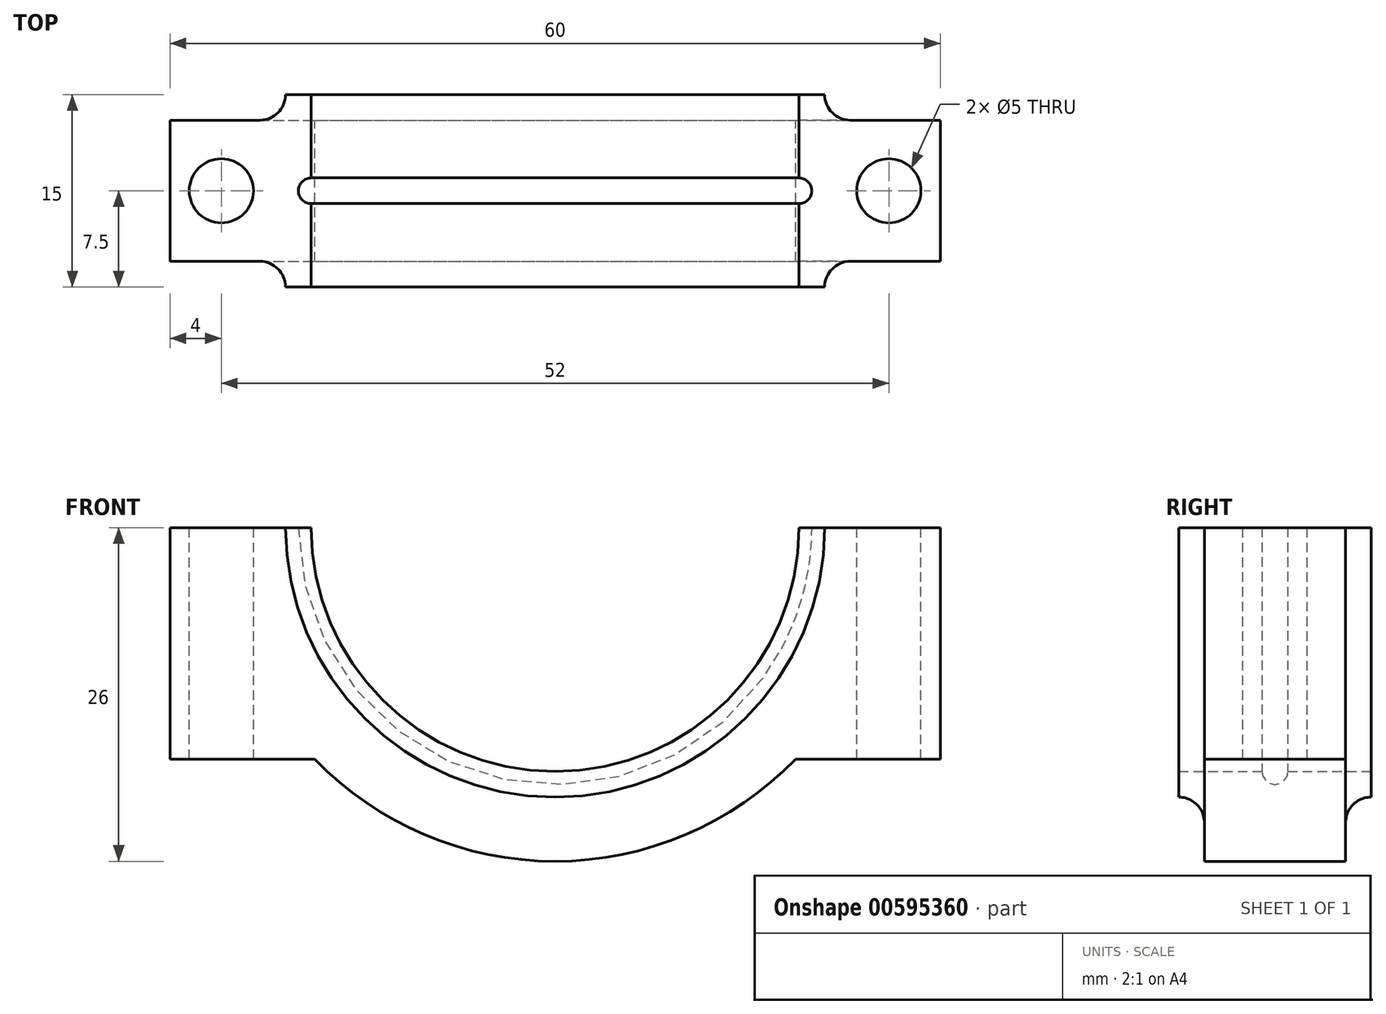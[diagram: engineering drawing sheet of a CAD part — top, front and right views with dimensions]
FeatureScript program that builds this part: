
annotation { "Feature Type Name" : "Feature", "Feature Type Description" : "" }
export const myFeature = defineFeature(function(context is Context, id is Id, definition is map)
    precondition{}
    {
        {
            var Q0;
            Q0=qCreatedBy(makeId("Front.planeOp"),FACE);
            var sketch = newSketch(context, id + "F0", { "sketchPlane" : qUnion([Q0])});
            skArc(sketch, "E0", {"start": v(-19, 0) * mm, "mid": v(0, -19) * mm, "end": v(19, 0) * mm});
            skLineSegment(sketch, "E1", {"start": v(-67.76, 0) * mm, "end": v(69.48, 0) * mm, "construction": true});
            skLineSegment(sketch, "E2", {"start": v(-30, 0) * mm, "end": v(-30, -18.03) * mm});
            skLineSegment(sketch, "E3.MirrorCS", {"start": v(30, 0) * mm, "end": v(30, -18.03) * mm});
            skLineSegment(sketch, "E4", {"start": v(-30, 0) * mm, "end": v(-19, 0) * mm});
            skLineSegment(sketch, "E5", {"start": v(19, 0) * mm, "end": v(30, 0) * mm});
            skArc(sketch, "E6", {"start": v(-18.73, -18.03) * mm, "mid": v(0, -26) * mm, "end": v(18.73, -18.03) * mm});
            skLineSegment(sketch, "E7", {"start": v(-30, -18.03) * mm, "end": v(-18.73, -18.03) * mm});
            skLineSegment(sketch, "E8", {"start": v(30, -18.03) * mm, "end": v(18.73, -18.03) * mm});
            skSolve(sketch);
        }
        {
            var Q0;
            Q0 = qSketchRegion(id + "F0", true);
            extrude(context, id + "F1", {"entities" : qUnion([Q0]), "endBound" : BoundingType.SYMMETRIC, "depth" : 11 * mm, "offsetDistance" : 25 * mm});
        }
        {
            var Q0;
            Q0=makeQuery(id+"F1.opExtrude","CAP_FACE",FACE,{"disambiguationData":[OSD([sQuery(id+"F0.wireOp",EDGE,"E0"),sQuery(id+"F0.wireOp",EDGE,"E2"),sQuery(id+"F0.wireOp",EDGE,"E3.MirrorCS"),sQuery(id+"F0.wireOp",EDGE,"E4"),sQuery(id+"F0.wireOp",EDGE,"E5"),sQuery(id+"F0.wireOp",EDGE,"E6"),sQuery(id+"F0.wireOp",EDGE,"E7"),sQuery(id+"F0.wireOp",EDGE,"E8")])],"isStart":false});
            var sketch = newSketch(context, id + "F2", { "sketchPlane" : qUnion([Q0])});
            skArc(sketch, "E9", {"start": v(-19, 0) * mm, "mid": v(0, -19) * mm, "end": v(19, 0) * mm});
            skArc(sketch, "E10", {"start": v(-21, 0) * mm, "mid": v(0, -21) * mm, "end": v(21, 0) * mm});
            skLineSegment(sketch, "E11", {"start": v(-26.55, 0) * mm, "end": v(28.6, 0) * mm, "construction": true});
            skLineSegment(sketch, "E12", {"start": v(-21, 0) * mm, "end": v(-19, 0) * mm});
            skLineSegment(sketch, "E13", {"start": v(19, 0) * mm, "end": v(21, 0) * mm});
            skSolve(sketch);
        }
        {
            var Q0;
            Q0 = qSketchRegion(id + "F2", true);
            extrude(context, id + "F3", {"entities" : qUnion([Q0]), "operationType" : NewBodyOperationType.ADD, "depth" : 2 * mm, "offsetDistance" : 25 * mm, "hasSecondDirection" : true, "secondDirectionOppositeDirection" : true, "secondDirectionDepth" : 13 * mm});
        }
        {
            var Q0;
            Q0=makeQuery(id+"F1.opExtrude","SWEPT_FACE",FACE,{"disambiguationData":[OSD([sQuery(id+"F0.wireOp",EDGE,"E4")])]});
            var sketch = newSketch(context, id + "F4", { "sketchPlane" : qUnion([Q0])});
            skCircle(sketch, "E14", {"center": v(-26, 0) * mm, "radius": 2.5 * mm});
            skCircle(sketch, "E15.MirrorC", {"center": v(26, 0) * mm, "radius": 2.5 * mm});
            skSolve(sketch);
        }
        {
            var Q0;
            Q0 = qSketchRegion(id + "F4", true);
            extrude(context, id + "F5", {"entities" : qUnion([Q0]), "operationType" : NewBodyOperationType.REMOVE, "endBound" : BoundingType.THROUGH_ALL, "oppositeDirection" : true, "depth" : 25 * mm, "offsetDistance" : 25 * mm});
        }
        {
            var Q0;
            Q0=makeQuery(id+"F3.boolean.opBoolean","INTERSECT",EDGE,{"derivedFrom":[makeQuery(id+"F1.opExtrude","CAP_FACE",FACE,{"disambiguationData":[OSD([sQuery(id+"F0.wireOp",EDGE,"E0"),sQuery(id+"F0.wireOp",EDGE,"E2"),sQuery(id+"F0.wireOp",EDGE,"E3.MirrorCS"),sQuery(id+"F0.wireOp",EDGE,"E4"),sQuery(id+"F0.wireOp",EDGE,"E5"),sQuery(id+"F0.wireOp",EDGE,"E6"),sQuery(id+"F0.wireOp",EDGE,"E7"),sQuery(id+"F0.wireOp",EDGE,"E8")])],"isStart":true}),makeQuery(id+"F3.opExtrude","SWEPT_FACE",FACE,{"disambiguationData":[OSD([sQuery(id+"F2.wireOp",EDGE,"E10")])]})]});
            fillet(context, id + "F6", {"entities" : qUnion([Q0]), "radius" : 2 * mm, "tangentPropagation" : true, "allowEdgeOverflow" : false});
        }
        {
            var Q0;
            Q0=makeQuery(id+"F3.boolean.opBoolean","INTERSECT",EDGE,{"derivedFrom":[makeQuery(id+"F1.opExtrude","CAP_FACE",FACE,{"disambiguationData":[OSD([sQuery(id+"F0.wireOp",EDGE,"E0"),sQuery(id+"F0.wireOp",EDGE,"E2"),sQuery(id+"F0.wireOp",EDGE,"E3.MirrorCS"),sQuery(id+"F0.wireOp",EDGE,"E4"),sQuery(id+"F0.wireOp",EDGE,"E5"),sQuery(id+"F0.wireOp",EDGE,"E6"),sQuery(id+"F0.wireOp",EDGE,"E7"),sQuery(id+"F0.wireOp",EDGE,"E8")])],"isStart":false}),makeQuery(id+"F3.opExtrude","SWEPT_FACE",FACE,{"disambiguationData":[OSD([sQuery(id+"F2.wireOp",EDGE,"E10")])]})]});
            fillet(context, id + "F7", {"entities" : qUnion([Q0]), "radius" : 2 * mm, "tangentPropagation" : true, "allowEdgeOverflow" : false});
        }
        {
            var Q0;
            Q0=makeQuery(id+"F3.boolean.opBoolean","MERGE",FACE,{"derivedFrom":[makeQuery(id+"F1.opExtrude","SWEPT_FACE",FACE,{"disambiguationData":[OSD([sQuery(id+"F0.wireOp",EDGE,"E4")])]}),makeQuery(id+"F3.opExtrude","SWEPT_FACE",FACE,{"disambiguationData":[OSD([sQuery(id+"F2.wireOp",EDGE,"E12")])]})]});
            var sketch = newSketch(context, id + "F8", { "sketchPlane" : qUnion([Q0])});
            skCircle(sketch, "E16", {"center": v(-19, 0) * mm, "radius": 1 * mm});
            skSolve(sketch);
        }
        {
            var Q0;
            Q0 = qSketchRegion(id + "F8", true);
            var Q1;
            Q1=makeQuery(id+"F3.boolean.opBoolean","MERGE",FACE,{"derivedFrom":[makeQuery(id+"F1.opExtrude","SWEPT_FACE",FACE,{"disambiguationData":[OSD([sQuery(id+"F0.wireOp",EDGE,"E0")])]}),makeQuery(id+"F3.opExtrude","SWEPT_FACE",FACE,{"disambiguationData":[OSD([sQuery(id+"F2.wireOp",EDGE,"E9")])]})]});
            revolve(context, id + "F9", {"operationType" : NewBodyOperationType.REMOVE, "entities" : qUnion([Q0]), "axis" : qUnion([Q1]), "revolveType" : RevolveType.FULL, "oppositeDirection" : true});
        }
    });
